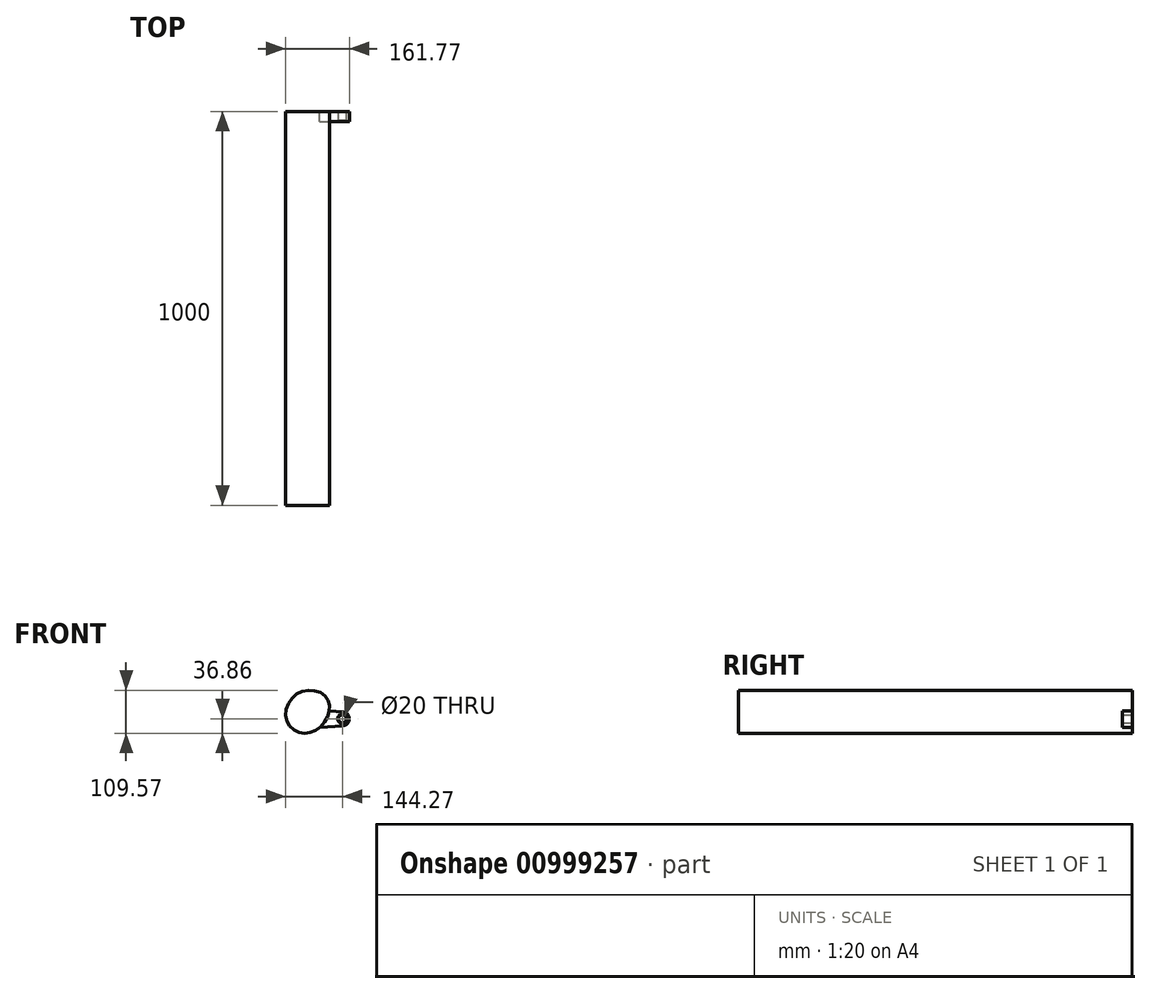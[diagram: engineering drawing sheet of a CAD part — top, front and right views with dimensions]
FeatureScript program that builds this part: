
annotation { "Feature Type Name" : "Feature", "Feature Type Description" : "" }
export const myFeature = defineFeature(function(context is Context, id is Id, definition is map)
    precondition{}
    {
        {
            var Q0;
            Q0=qCreatedBy(makeId("Front.planeOp"),FACE);
            var sketch = newSketch(context, id + "F0", { "sketchPlane" : qUnion([Q0])});
            skCircle(sketch, "E0", {"center": v(0, 0) * mm, "radius": 25 * mm});
            skCircle(sketch, "E1", {"center": v(90, 0) * mm, "radius": 17.5 * mm});
            skLineSegment(sketch, "E2", {"start": v(2.08, 24.91) * mm, "end": v(91.46, 17.44) * mm});
            skLineSegment(sketch, "E3", {"start": v(2.08, -24.91) * mm, "end": v(91.46, -17.44) * mm});
            skCircle(sketch, "E4", {"center": v(0, 0) * mm, "radius": 10 * mm});
            skCircle(sketch, "E5", {"center": v(90, 0) * mm, "radius": 10 * mm});
            skSolve(sketch);
        }
        {
            var Q0;
            Q0=qSketchRegion(id+"F0",true);
            extrude(context, id + "F1", {"entities" : qUnion([Q0]), "depth" : 25 * mm});
        }
        {
            var Q0;
            Q0=makeQuery(id+"F0.imprint","IMPRINT",FACE,{"disambiguationData":[TD([[makeQuery(id+"F0.imprint","IMPRINT",EDGE,{"derivedFrom":sQuery(id+"F0.wireOp",EDGE,"E4")}),-1.0]])]});
            extrude(context, id + "F2", {"entities" : qUnion([Q0]), "operationType" : NewBodyOperationType.ADD, "depth" : 50 * mm});
        }
        {
            var Q0;
            Q0=makeQuery(id+"F2.opExtrude","CAP_EDGE",EDGE,{"disambiguationData":[OSD([sQuery(id+"F0.wireOp",EDGE,"E0")])],"isStart":false});
            var Q1;
            Q1=makeQuery(id+"F2.opExtrude","CAP_EDGE",EDGE,{"disambiguationData":[OSD([sQuery(id+"F0.wireOp",EDGE,"E4")])],"isStart":false});
            var Q2;
            Q2=makeQuery(id+"F1.opExtrude","CAP_EDGE",EDGE,{"disambiguationData":[OSD([sQuery(id+"F0.wireOp",EDGE,"E5")])],"isStart":false});
            chamfer(context, id + "F3", {"entities" : qUnion([Q0, Q1, Q2]), "width" : 2 * mm, "tangentPropagation" : true});
        }
        {
            var Q0;
            Q0=qCreatedBy(makeId("Front.planeOp"),FACE);
            var sketch = newSketch(context, id + "F4", { "sketchPlane" : qUnion([Q0])});
            skFitSpline(sketch, "E6", {"points": [v(45.46, 58.3) * mm, v(-22.14, 65.55) * mm, v(-53.13, 0) * mm, v(-7.02, -36.84) * mm, v(50.36, 0) * mm, v(45.46, 58.3) * mm]});
            skSolve(sketch);
        }
        {
            var Q0;
            Q0 = qSketchRegion(id + "F4", true);
            extrude(context, id + "F5", {"entities" : qUnion([Q0]), "operationType" : NewBodyOperationType.ADD, "depth" : 1000 * mm, "offsetDistance" : 25 * mm});
        }
    });
